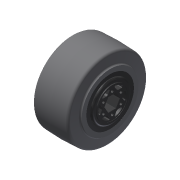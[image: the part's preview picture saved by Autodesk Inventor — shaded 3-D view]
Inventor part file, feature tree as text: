
AUTODESK INVENTOR PART (.ipt)
format: ipt  version: 2015 (Build 190159000, 159)  size: 1,915,904 bytes
history: native  units: in
note: dims shown in document units (in); Inventor stores cm internally (conversion verified against a paired STEP export)
features: revolve x1, other x1, extrude x1, mirror x1, imported_body x1, sketch x1, projected_geometry x1
ambient origin geometry x8: Origin, YZ Plane, XZ Plane, XY Plane, X Axis, Y Axis, Z Axis, Center Point
bodies: Body1 (feature_tree)
feature tree (7):
  revolve  "Revolve1"  [1 undecoded]
  other  "217-4050-STEP-201410301"
  extrude  "Extrusion1"  [1 undecoded]
  mirror  "Mirror1"
  imported_body  "Base1"
  sketch  "Sketch1"  dims[d0=1.7717in d1=0.0039in d2=0.0in]
  projected_geometry  "Projected Loop1"
note: 2 required parameter values undecoded (feature->parameter linkage not recoverable at this tier; creation-order binding heuristic only, values carry confidence <= 0.55)